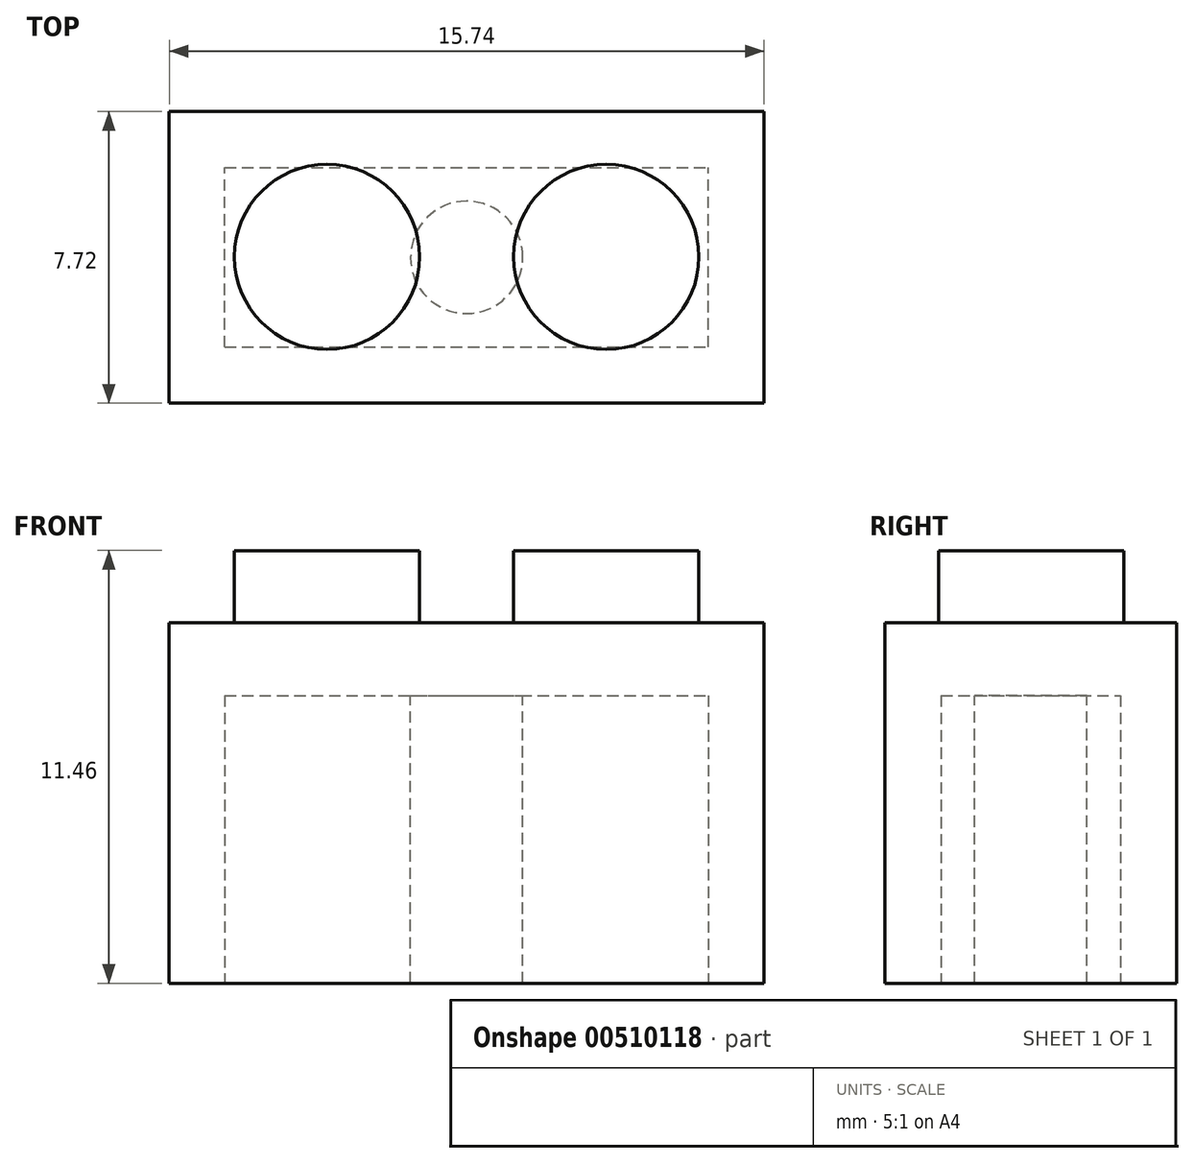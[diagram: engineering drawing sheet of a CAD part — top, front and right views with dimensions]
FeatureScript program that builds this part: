
annotation { "Feature Type Name" : "Feature", "Feature Type Description" : "" }
export const myFeature = defineFeature(function(context is Context, id is Id, definition is map)
    precondition{}
    {
        {
            var Q0;
            Q0=qCreatedBy(makeId("Top.planeOp"),FACE);
            var sketch = newSketch(context, id + "F0", { "sketchPlane" : qUnion([Q0])});
            skLineSegment(sketch, "E0.bottom", {"start": v(-7.87, 3.86) * mm, "end": v(7.87, 3.86) * mm});
            skLineSegment(sketch, "E0.top", {"start": v(-7.87, -3.86) * mm, "end": v(7.87, -3.86) * mm});
            skLineSegment(sketch, "E0.left", {"start": v(-7.87, 3.86) * mm, "end": v(-7.87, -3.86) * mm});
            skLineSegment(sketch, "E0.right", {"start": v(7.87, 3.86) * mm, "end": v(7.87, -3.86) * mm});
            skPoint(sketch, "E0.middle", {"position": v(0, 0) * mm});
            skSolve(sketch);
        }
        {
            var Q0;
            Q0=makeQuery(id+"F0.imprint","IMPRINT",FACE,{"disambiguationData":[TD([[makeQuery(id+"F0.imprint","IMPRINT",EDGE,{"derivedFrom":sQuery(id+"F0.wireOp",EDGE,"E0.bottom")}),-1.0]])]});
            extrude(context, id + "F1", {"entities" : qUnion([Q0]), "depth" : 9.55 * mm});
        }
        {
            var Q0;
            Q0=makeQuery(id+"F1.opExtrude","CAP_FACE",FACE,{"disambiguationData":[OSD([sQuery(id+"F0.wireOp",EDGE,"E0.bottom"),sQuery(id+"F0.wireOp",EDGE,"E0.top"),sQuery(id+"F0.wireOp",EDGE,"E0.left"),sQuery(id+"F0.wireOp",EDGE,"E0.right")])],"isStart":false});
            var sketch = newSketch(context, id + "F2", { "sketchPlane" : qUnion([Q0])});
            skCircle(sketch, "E1", {"center": v(-3.7, 0.01) * mm, "radius": 2.45 * mm});
            skSolve(sketch);
        }
        {
            var Q0;
            Q0 = qSketchRegion(id + "F2", true);
            extrude(context, id + "F3", {"entities" : qUnion([Q0]), "operationType" : NewBodyOperationType.ADD, "depth" : 1.9 * mm});
        }
        {
            var Q0;
            Q0=makeQuery(id+"F1.opExtrude","CAP_FACE",FACE,{"disambiguationData":[OSD([sQuery(id+"F0.wireOp",EDGE,"E0.bottom"),sQuery(id+"F0.wireOp",EDGE,"E0.top"),sQuery(id+"F0.wireOp",EDGE,"E0.left"),sQuery(id+"F0.wireOp",EDGE,"E0.right")])],"isStart":false});
            var sketch = newSketch(context, id + "F4", { "sketchPlane" : qUnion([Q0])});
            skCircle(sketch, "E2", {"center": v(3.7, 0.01) * mm, "radius": 2.45 * mm});
            skSolve(sketch);
        }
        {
            var Q0;
            Q0 = qSketchRegion(id + "F4", true);
            extrude(context, id + "F5", {"entities" : qUnion([Q0]), "operationType" : NewBodyOperationType.ADD, "depth" : 1.9 * mm});
        }
        {
            var Q0;
            Q0=makeQuery(id+"F1.opExtrude","CAP_FACE",FACE,{"disambiguationData":[OSD([sQuery(id+"F0.wireOp",EDGE,"E0.bottom"),sQuery(id+"F0.wireOp",EDGE,"E0.top"),sQuery(id+"F0.wireOp",EDGE,"E0.left"),sQuery(id+"F0.wireOp",EDGE,"E0.right")])],"isStart":true});
            var sketch = newSketch(context, id + "F6", { "sketchPlane" : qUnion([Q0])});
            skLineSegment(sketch, "E3.bottom", {"start": v(-6.4, 2.37) * mm, "end": v(6.4, 2.37) * mm});
            skLineSegment(sketch, "E3.top", {"start": v(-6.4, -2.37) * mm, "end": v(6.4, -2.37) * mm});
            skLineSegment(sketch, "E3.left", {"start": v(-6.4, 2.37) * mm, "end": v(-6.4, -2.37) * mm});
            skLineSegment(sketch, "E3.right", {"start": v(6.4, 2.37) * mm, "end": v(6.4, -2.37) * mm});
            skPoint(sketch, "E3.middle", {"position": v(0, 0) * mm});
            skSolve(sketch);
        }
        {
            var Q0;
            Q0=makeQuery(id+"F6.imprint","IMPRINT",FACE,{"disambiguationData":[TD([[makeQuery(id+"F6.imprint","IMPRINT",EDGE,{"derivedFrom":sQuery(id+"F6.wireOp",EDGE,"E3.bottom")}),-1.0]])]});
            extrude(context, id + "F7", {"entities" : qUnion([Q0]), "operationType" : NewBodyOperationType.REMOVE, "oppositeDirection" : true, "depth" : 7.62 * mm});
        }
        {
            var Q0;
            Q0=makeQuery(id+"F7.boolean.opBoolean","COPY",FACE,{"derivedFrom":makeQuery(id+"F7.opExtrude","CAP_FACE",FACE,{"disambiguationData":[OSD([sQuery(id+"F6.wireOp",EDGE,"E3.bottom"),sQuery(id+"F6.wireOp",EDGE,"E3.top"),sQuery(id+"F6.wireOp",EDGE,"E3.left"),sQuery(id+"F6.wireOp",EDGE,"E3.right")])],"isStart":false})});
            var sketch = newSketch(context, id + "F8", { "sketchPlane" : qUnion([Q0])});
            skCircle(sketch, "E4", {"center": v(0, 0) * mm, "radius": 1.49 * mm});
            skSolve(sketch);
        }
        {
            var Q0;
            Q0=makeQuery(id+"F8.imprint","IMPRINT",FACE,{"disambiguationData":[TD([[makeQuery(id+"F8.imprint","IMPRINT",EDGE,{"derivedFrom":sQuery(id+"F8.wireOp",EDGE,"E4")}),1.0]])]});
            extrude(context, id + "F9", {"entities" : qUnion([Q0]), "operationType" : NewBodyOperationType.ADD, "depth" : 7.62 * mm});
        }
    });
